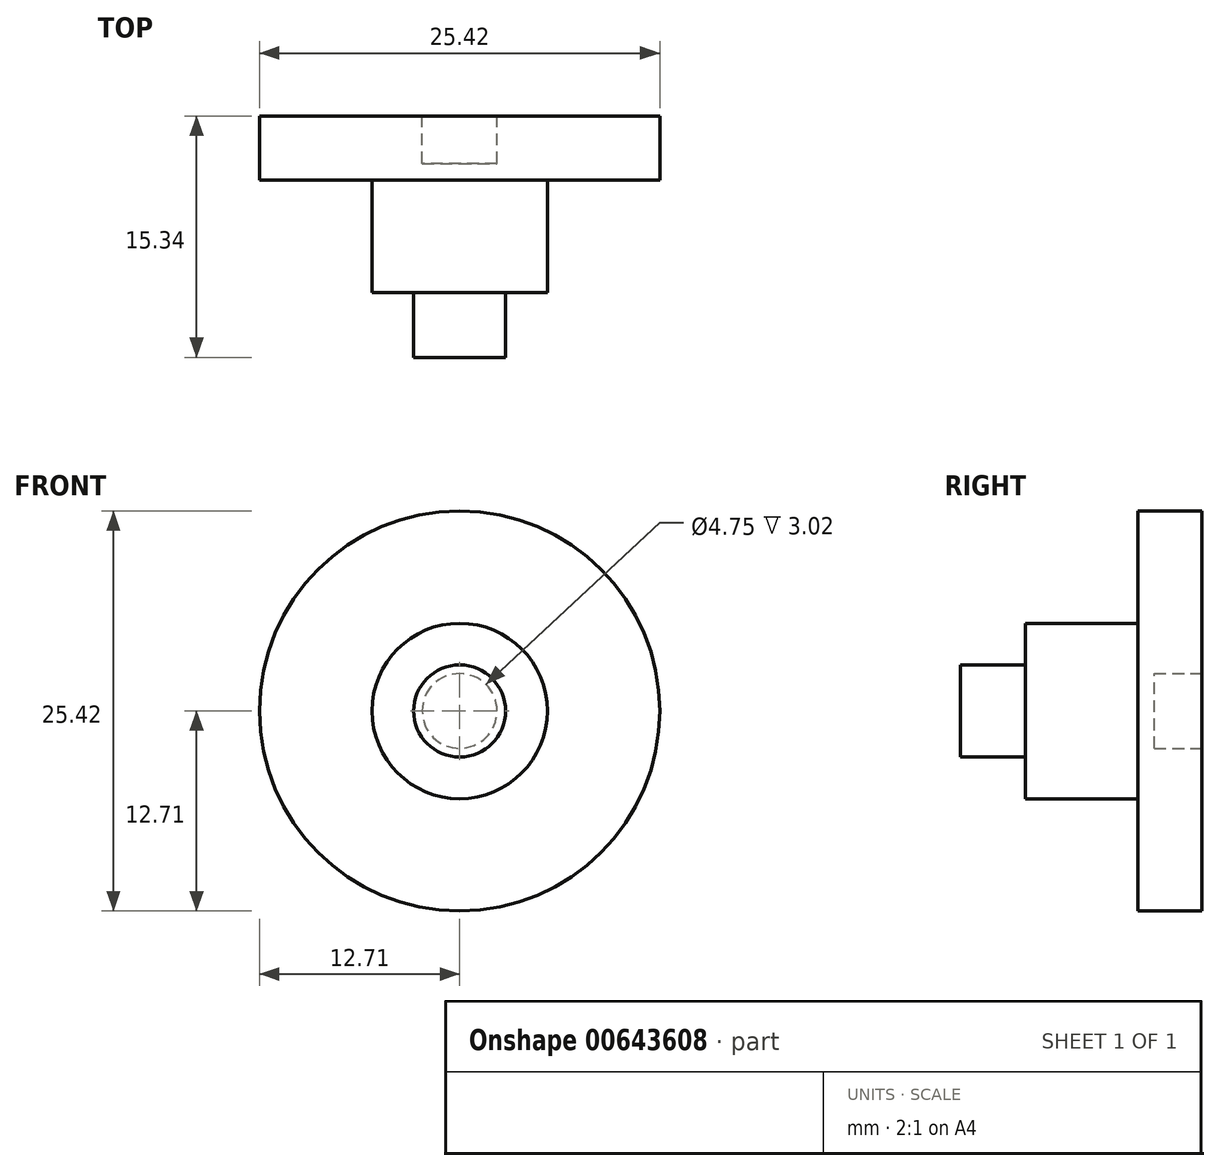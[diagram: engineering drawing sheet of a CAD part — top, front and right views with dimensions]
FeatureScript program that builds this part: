
annotation { "Feature Type Name" : "Feature", "Feature Type Description" : "" }
export const myFeature = defineFeature(function(context is Context, id is Id, definition is map)
    precondition{}
    {
        {
            var Q0;
            Q0=qCreatedBy(makeId("Front.planeOp"),FACE);
            var sketch = newSketch(context, id + "F0", { "sketchPlane" : qUnion([Q0])});
            skCircle(sketch, "E0", {"center": v(0, 0) * mm, "radius": 12.71 * mm});
            skSolve(sketch);
        }
        {
            var Q0;
            Q0 = qSketchRegion(id + "F0", true);
            var Q1;
            Q1 = qConstructionFilter(qBodyType(qCreatedBy(id + "F0" ,EDGE), BodyType.WIRE), ConstructionObject.NO);
            extrude(context, id + "F1", {"entities" : qUnion([Q0]), "surfaceEntities" : qUnion([Q1]), "depth" : 4.07 * mm, "offsetDistance" : 25.4 * mm});
        }
        {
            var Q0;
            Q0=qCreatedBy(makeId("Front.planeOp"),FACE);
            var sketch = newSketch(context, id + "F2", { "sketchPlane" : qUnion([Q0])});
            skCircle(sketch, "E1", {"center": v(0, 0) * mm, "radius": 5.57 * mm});
            skSolve(sketch);
        }
        {
            var Q0;
            Q0 = qSketchRegion(id + "F2", true);
            extrude(context, id + "F3", {"entities" : qUnion([Q0]), "operationType" : NewBodyOperationType.ADD, "depth" : 11.22 * mm, "offsetDistance" : 25.4 * mm});
        }
        {
            var Q0;
            Q0=makeQuery(id+"F3.opExtrude","CAP_FACE",FACE,{"disambiguationData":[OSD([sQuery(id+"F2.wireOp",EDGE,"E1")])],"isStart":false});
            var sketch = newSketch(context, id + "F4", { "sketchPlane" : qUnion([Q0])});
            skCircle(sketch, "E2", {"center": v(0, 0) * mm, "radius": 2.92 * mm});
            skSolve(sketch);
        }
        {
            var Q0;
            Q0 = qSketchRegion(id + "F4", true);
            extrude(context, id + "F5", {"entities" : qUnion([Q0]), "operationType" : NewBodyOperationType.ADD, "depth" : 4.12 * mm, "offsetDistance" : 25.4 * mm});
        }
        {
            var Q0;
            Q0=makeQuery(id+"F0.imprint","IMPRINT",FACE,{"disambiguationData":[TD([[makeQuery(id+"F0.imprint","IMPRINT",EDGE,{"derivedFrom":sQuery(id+"F0.wireOp",EDGE,"E0")}),1.0]])]});
            var sketch = newSketch(context, id + "F6", { "sketchPlane" : qUnion([Q0])});
            skCircle(sketch, "E3", {"center": v(0, 0) * mm, "radius": 2.38 * mm});
            skSolve(sketch);
        }
        {
            var Q0;
            Q0 = qSketchRegion(id + "F6", true);
            extrude(context, id + "F7", {"entities" : qUnion([Q0]), "operationType" : NewBodyOperationType.REMOVE, "endBound" : BoundingType.SYMMETRIC, "depth" : 6.04 * mm, "offsetDistance" : 25.4 * mm});
        }
    });
